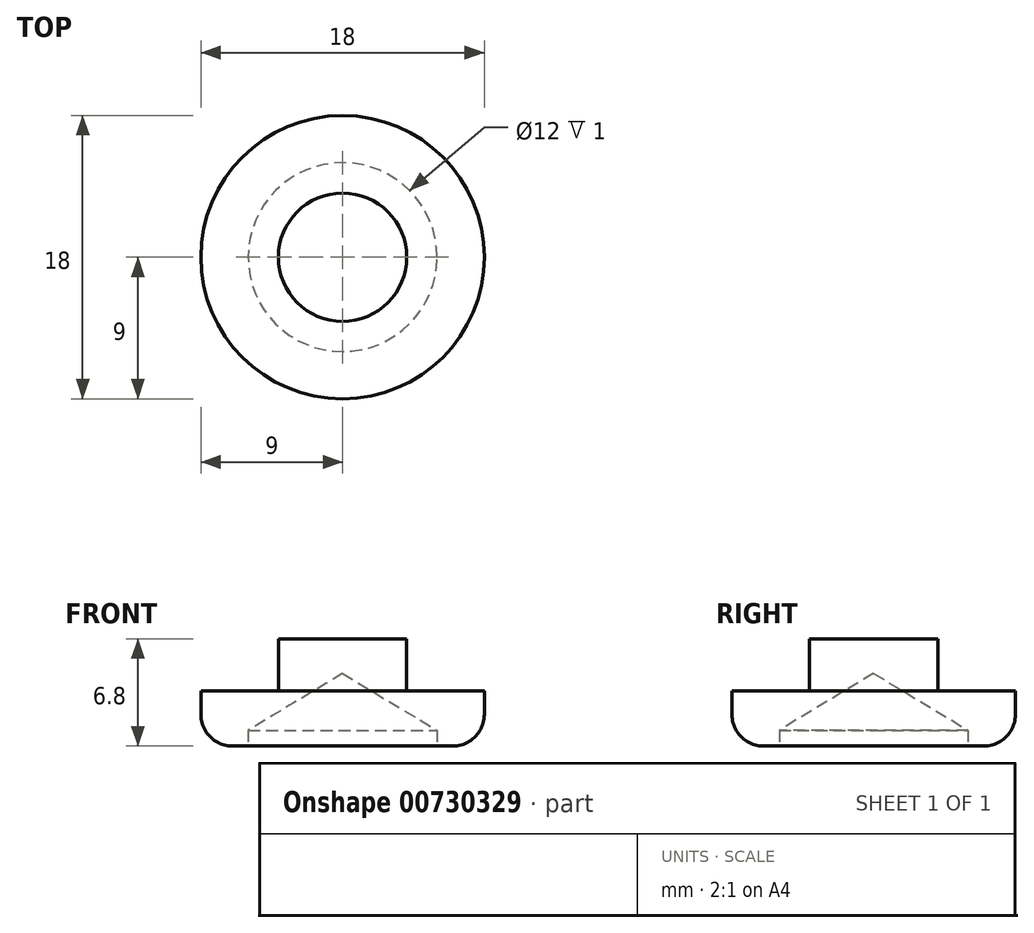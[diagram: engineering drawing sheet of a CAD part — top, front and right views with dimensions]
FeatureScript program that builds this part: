
annotation { "Feature Type Name" : "Feature", "Feature Type Description" : "" }
export const myFeature = defineFeature(function(context is Context, id is Id, definition is map)
    precondition{}
    {
        {
            var Q0;
            Q0=qCreatedBy(makeId("Top.planeOp"),FACE);
            var sketch = newSketch(context, id + "F0", { "sketchPlane" : qUnion([Q0])});
            skCircle(sketch, "E0", {"center": v(0, 0) * mm, "radius": 4.08 * mm});
            skCircle(sketch, "E1", {"center": v(0, 0) * mm, "radius": 9 * mm});
            skPoint(sketch, "E2.center", {"position": v(0, 0.1) * mm});
            skSolve(sketch);
        }
        {
            var Q0;
            Q0=makeQuery(id+"F0.imprint","IMPRINT",FACE,{"disambiguationData":[TD([[makeQuery(id+"F0.imprint","IMPRINT",EDGE,{"derivedFrom":sQuery(id+"F0.wireOp",EDGE,"E0")}),1.0]])]});
            extrude(context, id + "F1", {"entities" : qUnion([Q0]), "depth" : 6.8 * mm, "offsetDistance" : 25 * mm});
        }
        {
            var Q0;
            Q0=makeQuery(id+"F0.imprint","IMPRINT",FACE,{"disambiguationData":[TD([[makeQuery(id+"F0.imprint","IMPRINT",EDGE,{"derivedFrom":sQuery(id+"F0.wireOp",EDGE,"E0")}),-1.0]])]});
            extrude(context, id + "F2", {"entities" : qUnion([Q0]), "operationType" : NewBodyOperationType.ADD, "depth" : 3.5 * mm, "offsetDistance" : 25 * mm});
        }
        {
            var Q0;
            Q0=makeQuery(id+"F2.opExtrude","CAP_EDGE",EDGE,{"disambiguationData":[OSD([sQuery(id+"F0.wireOp",EDGE,"E1")])],"isStart":true});
            fillet(context, id + "F3", {"entities" : qUnion([Q0]), "radius" : 2 * mm, "tangentPropagation" : true, "allowEdgeOverflow" : false});
        }
        {
            var Q0;
            Q0=sQuery(id+"F0.wireOp",VERTEX,"E0.center");
            var Q1;
            Q1=makeQuery(id+"F1.opExtrude","SWEPT_BODY",BODY,{"disambiguationData":[OSD([sQuery(id+"F0.wireOp",EDGE,"E0")])]});
            hole(context, id + "F4", {"style" : HoleStyle.SIMPLE, "endStyle" : HoleEndStyle.BLIND, "oppositeDirection" : true, "holeDiameter" : 12 * mm, "majorDiameter" : 5 * mm, "holeDepth" : 1 * mm, "isTappedThrough" : true, "tappedDepth" : 12 * mm, "tapClearance" : 3, "locations" : qUnion([Q0]), "scope" : qUnion([Q1])});
        }
    });
